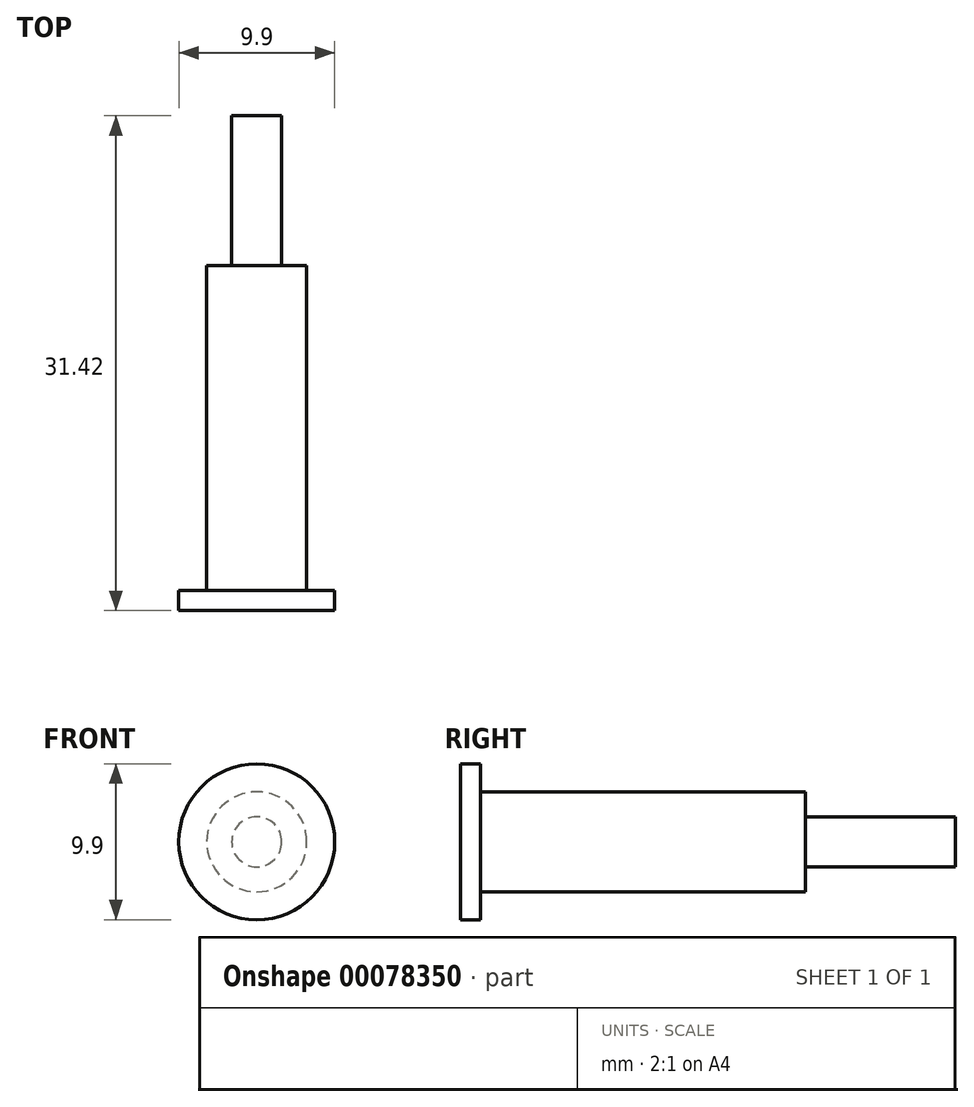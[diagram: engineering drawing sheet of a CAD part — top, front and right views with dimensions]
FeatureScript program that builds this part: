
annotation { "Feature Type Name" : "Feature", "Feature Type Description" : "" }
export const myFeature = defineFeature(function(context is Context, id is Id, definition is map)
    precondition{}
    {
        {
            var Q0;
            Q0=qCreatedBy(makeId("Right.planeOp"),FACE);
            var sketch = newSketch(context, id + "F0", { "sketchPlane" : qUnion([Q0])});
            skLineSegment(sketch, "E0", {"start": v(0, 0) * mm, "end": v(0, 4.95) * mm});
            skLineSegment(sketch, "E1", {"start": v(0, 4.95) * mm, "end": v(1.27, 4.95) * mm});
            skLineSegment(sketch, "E2", {"start": v(1.27, 3.18) * mm, "end": v(21.9, 3.18) * mm});
            skLineSegment(sketch, "E3", {"start": v(0, 0) * mm, "end": v(31.42, 0) * mm});
            skLineSegment(sketch, "E4", {"start": v(31.42, 0) * mm, "end": v(31.42, 1.59) * mm});
            skLineSegment(sketch, "E5", {"start": v(31.42, 1.59) * mm, "end": v(21.9, 1.59) * mm});
            skLineSegment(sketch, "E6", {"start": v(21.9, 3.18) * mm, "end": v(21.9, 1.59) * mm});
            skLineSegment(sketch, "E7", {"start": v(1.27, 4.95) * mm, "end": v(1.27, 3.18) * mm});
            skSolve(sketch);
        }
        {
            var Q0;
            Q0 = qSketchRegion(id + "F0", true);
            var Q1;
            Q1=sQuery(id+"F0.wireOp",EDGE,"E3");
            revolve(context, id + "F1", {"entities" : qUnion([Q0]), "axis" : qUnion([Q1]), "revolveType" : RevolveType.FULL});
        }
    });
